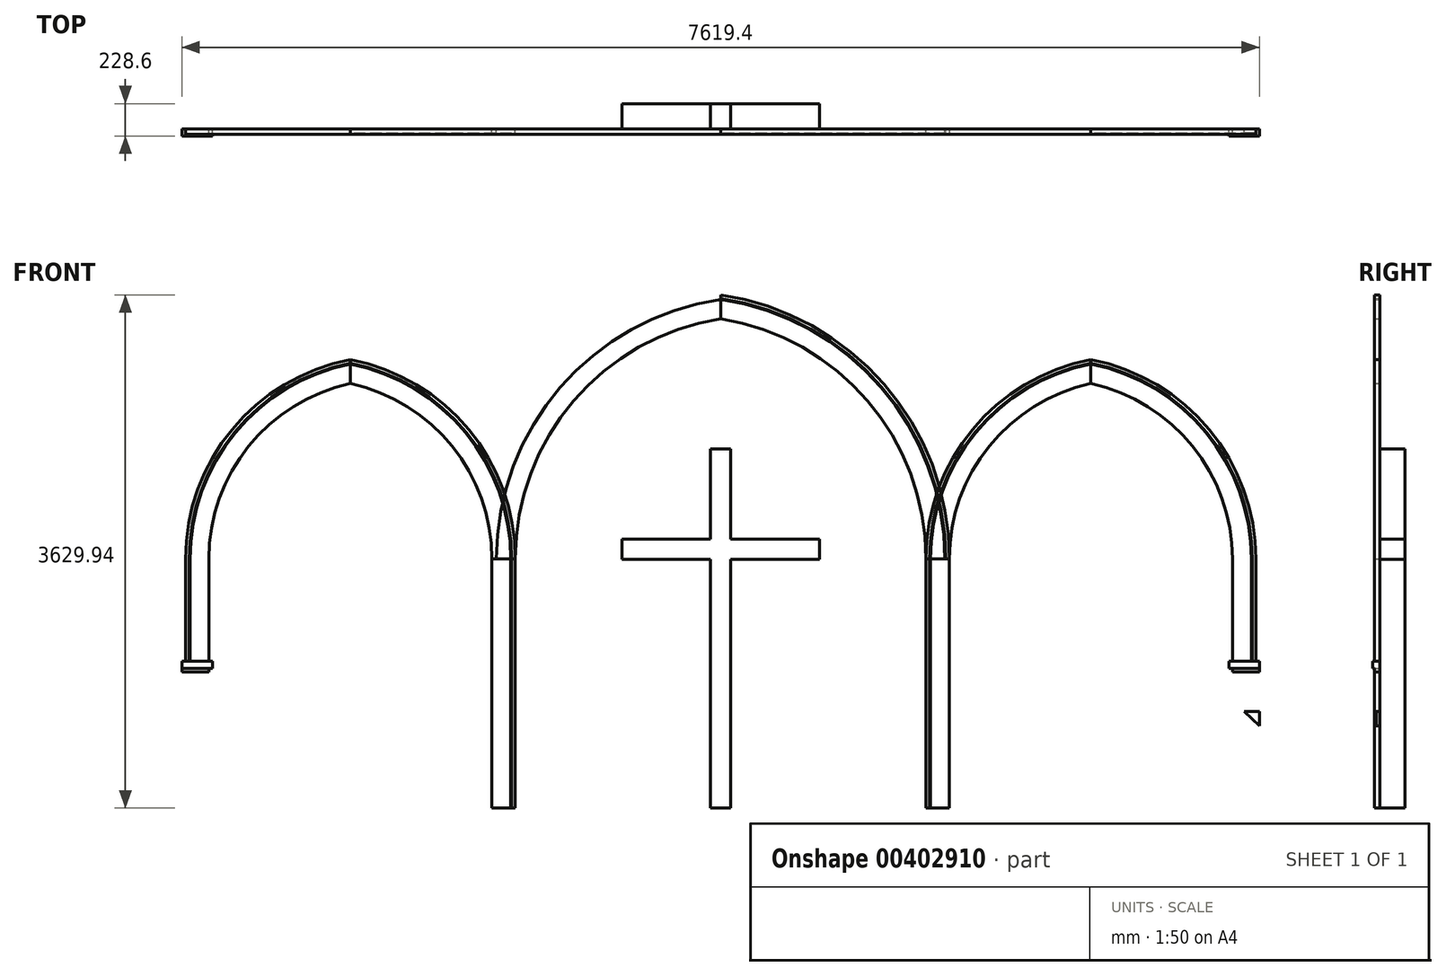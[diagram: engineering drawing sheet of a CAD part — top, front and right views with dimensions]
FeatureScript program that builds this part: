
annotation { "Feature Type Name" : "Feature", "Feature Type Description" : "" }
export const myFeature = defineFeature(function(context is Context, id is Id, definition is map)
    precondition{}
    {
        {
            var Q0;
            Q0=qCreatedBy(makeId("Front.planeOp"),FACE);
            var sketch = newSketch(context, id + "F0", { "sketchPlane" : qUnion([Q0])});
            skLineSegment(sketch, "E0", {"start": v(0, 0) * mm, "end": v(986.7, 0) * mm, "construction": true});
            skLineSegment(sketch, "E1", {"start": v(986.7, 0) * mm, "end": v(986.7, 0) * mm});
            skArc(sketch, "E2", {"start": v(986.7, 0) * mm, "mid": v(709.41, 787.09) * mm, "end": v(0, 1226.56) * mm, "construction": true});
            skLineSegment(sketch, "E3", {"start": v(0, 0) * mm, "end": v(0, 1226.56) * mm, "construction": true});
            skArc(sketch, "E4", {"start": v(1120.06, 0) * mm, "mid": v(804.11, 882) * mm, "end": v(0, 1362.77) * mm, "construction": true});
            skArc(sketch, "E5", {"start": v(1126.4, 0) * mm, "mid": v(808.62, 886.51) * mm, "end": v(0, 1369.24) * mm, "construction": true});
            skArc(sketch, "E6", {"start": v(1151.8, 0) * mm, "mid": v(826.65, 904.57) * mm, "end": v(0, 1395.11) * mm, "construction": true});
            skLineSegment(sketch, "E7", {"start": v(986.7, 0) * mm, "end": v(1120.06, 0) * mm, "construction": true});
            skLineSegment(sketch, "E8", {"start": v(1120.06, 0) * mm, "end": v(1126.4, 0) * mm, "construction": true});
            skLineSegment(sketch, "E9", {"start": v(1126.4, 0) * mm, "end": v(1151.8, 0) * mm, "construction": true});
            skSolve(sketch);
        }
        {
            var Q0;
            Q0=qCreatedBy(makeId("Front.planeOp"),FACE);
            var sketch = newSketch(context, id + "F1", { "sketchPlane" : qUnion([Q0])});
            skArc(sketch, "E10", {"start": v(1452.06, 0) * mm, "mid": v(1039.63, 1117.83) * mm, "end": v(0, 1699.91) * mm});
            skArc(sketch, "E11", {"start": v(1585.41, 0) * mm, "mid": v(1134.15, 1212.44) * mm, "end": v(0, 1834.8) * mm});
            skArc(sketch, "E12", {"start": v(1591.76, 0) * mm, "mid": v(1138.65, 1216.94) * mm, "end": v(0, 1841.22) * mm});
            skArc(sketch, "E13", {"start": v(1617.16, 0) * mm, "mid": v(1156.65, 1234.96) * mm, "end": v(0, 1866.89) * mm});
            skLineSegment(sketch, "E14", {"start": v(1452.06, 0) * mm, "end": v(1585.41, 0) * mm, "construction": true});
            skLineSegment(sketch, "E15", {"start": v(1585.41, 0) * mm, "end": v(1591.76, 0) * mm, "construction": true});
            skLineSegment(sketch, "E16", {"start": v(1591.76, 0) * mm, "end": v(1617.16, 0) * mm, "construction": true});
            skLineSegment(sketch, "E17", {"start": v(0, 1866.89) * mm, "end": v(0, 1699.91) * mm});
            skLineSegment(sketch, "E18", {"start": v(1452.06, 0) * mm, "end": v(1617.16, 0) * mm});
            skSolve(sketch);
        }
        {
            var Q0;
            Q0=qCreatedBy(makeId("Front.planeOp"),FACE);
            var sketch = newSketch(context, id + "F2", { "sketchPlane" : qUnion([Q0])});
            skLineSegment(sketch, "E19.bottom", {"start": v(71.44, 776.95) * mm, "end": v(-71.44, 776.95) * mm});
            skLineSegment(sketch, "E19.top", {"start": v(71.44, -1763.05) * mm, "end": v(-71.44, -1763.05) * mm});
            skLineSegment(sketch, "E19.left", {"start": v(71.44, 776.95) * mm, "end": v(71.44, -1763.05) * mm});
            skLineSegment(sketch, "E19.right", {"start": v(-71.44, 776.95) * mm, "end": v(-71.44, -1763.05) * mm});
            skPoint(sketch, "E19.middle", {"position": v(0, -493.05) * mm});
            skLineSegment(sketch, "E20.bottom", {"start": v(698.5, 138.78) * mm, "end": v(-698.5, 138.78) * mm});
            skLineSegment(sketch, "E20.top", {"start": v(698.5, -4.1) * mm, "end": v(-698.5, -4.1) * mm});
            skLineSegment(sketch, "E20.left", {"start": v(698.5, 138.78) * mm, "end": v(698.5, -4.1) * mm});
            skLineSegment(sketch, "E20.right", {"start": v(-698.5, 138.78) * mm, "end": v(-698.5, -4.1) * mm});
            skPoint(sketch, "E20.middle", {"position": v(0, 67.34) * mm});
            skSolve(sketch);
        }
        {
            var Q0;
            Q0=qCreatedBy(makeId("Front.planeOp"),FACE);
            var sketch = newSketch(context, id + "F3", { "sketchPlane" : qUnion([Q0])});
            skLineSegment(sketch, "E21", {"start": v(2618.18, 0) * mm, "end": v(3604.88, 0) * mm, "construction": true});
            skArc(sketch, "E22", {"start": v(3604.88, 0) * mm, "mid": v(3327.6, 787.09) * mm, "end": v(2618.18, 1226.56) * mm, "construction": true});
            skLineSegment(sketch, "E23", {"start": v(2618.18, 0) * mm, "end": v(2618.18, 1226.56) * mm, "construction": true});
            skArc(sketch, "E24", {"start": v(3738.23, 0) * mm, "mid": v(3422.29, 882) * mm, "end": v(2618.18, 1362.77) * mm, "construction": true});
            skArc(sketch, "E25", {"start": v(3744.58, 0) * mm, "mid": v(3426.8, 886.51) * mm, "end": v(2618.18, 1369.24) * mm, "construction": true});
            skArc(sketch, "E26", {"start": v(3769.98, 0) * mm, "mid": v(3444.83, 904.57) * mm, "end": v(2618.18, 1395.11) * mm, "construction": true});
            skLineSegment(sketch, "E27", {"start": v(3604.88, 0) * mm, "end": v(3738.23, 0) * mm, "construction": true});
            skLineSegment(sketch, "E28", {"start": v(3738.23, 0) * mm, "end": v(3744.58, 0) * mm, "construction": true});
            skLineSegment(sketch, "E29", {"start": v(3744.58, 0) * mm, "end": v(3769.98, 0) * mm, "construction": true});
            skLineSegment(sketch, "E30", {"start": v(2349.17, 0) * mm, "end": v(2618.18, 0) * mm, "construction": true});
            skLineSegment(sketch, "E31", {"start": v(2618.18, 1226.56) * mm, "end": v(2618.18, 1362.77) * mm, "construction": true});
            skLineSegment(sketch, "E32", {"start": v(2618.18, 1362.77) * mm, "end": v(2618.18, 1369.24) * mm, "construction": true});
            skLineSegment(sketch, "E33", {"start": v(2618.18, 1369.24) * mm, "end": v(2618.18, 1395.11) * mm, "construction": true});
            skArc(sketch, "E34", {"start": v(3619.2, 0) * mm, "mid": v(3337.76, 797.28) * mm, "end": v(2618.18, 1241.2) * mm});
            skArc(sketch, "E35", {"start": v(3752.55, 0) * mm, "mid": v(3432.45, 892.17) * mm, "end": v(2618.18, 1377.35) * mm});
            skArc(sketch, "E36", {"start": v(3758.9, 0) * mm, "mid": v(3436.96, 896.69) * mm, "end": v(2618.18, 1383.82) * mm});
            skArc(sketch, "E37", {"start": v(3784.3, 0) * mm, "mid": v(3454.98, 914.75) * mm, "end": v(2618.18, 1409.69) * mm});
            skLineSegment(sketch, "E38", {"start": v(3619.2, 0) * mm, "end": v(3752.55, 0) * mm, "construction": true});
            skLineSegment(sketch, "E39", {"start": v(3752.55, 0) * mm, "end": v(3758.9, 0) * mm, "construction": true});
            skLineSegment(sketch, "E40", {"start": v(3758.9, 0) * mm, "end": v(3784.3, 0) * mm, "construction": true});
            skLineSegment(sketch, "E41", {"start": v(3619.2, 0) * mm, "end": v(3784.3, 0) * mm});
            skLineSegment(sketch, "E42", {"start": v(2618.18, 1241.2) * mm, "end": v(2618.18, 1409.69) * mm});
            skLineSegment(sketch, "E43", {"start": v(2618.18, -162.35) * mm, "end": v(3784.3, -162.35) * mm, "construction": true});
            skLineSegment(sketch, "E44", {"start": v(2618.18, 0) * mm, "end": v(1452.06, 0) * mm, "construction": true});
            skPoint(sketch, "E44.endSnap0", {"position": v(2483.68, 0) * mm});
            skSolve(sketch);
        }
        {
            var Q0;
            {var subQ0=sQuery(id+"F1.wireOp",EDGE,"E10");Q0=makeQuery(id+"F1.imprint","IMPRINT",FACE,{"disambiguationData":[TD([[makeQuery(id+"F1.imprint","IMPRINT",EDGE,{"derivedFrom":subQ0}),-1.0]])]});}
            var Q1;
            {var subQ0=sQuery(id+"F1.wireOp",EDGE,"E12");Q1=makeQuery(id+"F1.imprint","IMPRINT",FACE,{"disambiguationData":[TD([[makeQuery(id+"F1.imprint","IMPRINT",EDGE,{"derivedFrom":subQ0}),-1.0]])]});}
            extrude(context, id + "F4", {"entities" : qUnion([Q0, Q1]), "depth" : 38.1 * mm});
        }
        {
            var Q0;
            {var subQ0=sQuery(id+"F1.wireOp",EDGE,"E11");Q0=makeQuery(id+"F1.imprint","IMPRINT",FACE,{"disambiguationData":[TD([[makeQuery(id+"F1.imprint","IMPRINT",EDGE,{"derivedFrom":subQ0}),-1.0]])]});}
            extrude(context, id + "F5", {"entities" : qUnion([Q0]), "depth" : 31.75 * mm});
        }
        {
            var Q0;
            {var subQ0=sQuery(id+"F3.wireOp",EDGE,"E36");Q0=makeQuery(id+"F3.imprint","IMPRINT",FACE,{"disambiguationData":[TD([[makeQuery(id+"F3.imprint","IMPRINT",EDGE,{"derivedFrom":subQ0}),-1.0]])]});}
            var Q1;
            {var subQ0=sQuery(id+"F3.wireOp",EDGE,"E34");Q1=makeQuery(id+"F3.imprint","IMPRINT",FACE,{"disambiguationData":[TD([[makeQuery(id+"F3.imprint","IMPRINT",EDGE,{"derivedFrom":subQ0}),-1.0]])]});}
            extrude(context, id + "F6", {"entities" : qUnion([Q0, Q1]), "depth" : 38.1 * mm});
        }
        {
            var Q0;
            {var subQ0=sQuery(id+"F3.wireOp",EDGE,"E35");Q0=makeQuery(id+"F3.imprint","IMPRINT",FACE,{"disambiguationData":[TD([[makeQuery(id+"F3.imprint","IMPRINT",EDGE,{"derivedFrom":subQ0}),-1.0]])]});}
            extrude(context, id + "F7", {"entities" : qUnion([Q0]), "depth" : 31.75 * mm});
        }
        {
            var Q0;
            Q0=makeQuery(id+"F6.opExtrude","SWEPT_BODY",BODY,{"disambiguationData":[OSD([sQuery(id+"F3.wireOp",EDGE,"E34"),sQuery(id+"F3.wireOp",EDGE,"E35"),sQuery(id+"F3.wireOp",EDGE,"E41"),sQuery(id+"F3.wireOp",EDGE,"E42")])]});
            var Q1;
            Q1=makeQuery(id+"F6.opExtrude","SWEPT_BODY",BODY,{"disambiguationData":[OSD([sQuery(id+"F3.wireOp",EDGE,"E36"),sQuery(id+"F3.wireOp",EDGE,"E37"),sQuery(id+"F3.wireOp",EDGE,"E41"),sQuery(id+"F3.wireOp",EDGE,"E42")])]});
            var Q2;
            Q2=makeQuery(id+"F7.opExtrude","SWEPT_BODY",BODY,{"disambiguationData":[OSD([sQuery(id+"F3.wireOp",EDGE,"E35"),sQuery(id+"F3.wireOp",EDGE,"E36"),sQuery(id+"F3.wireOp",EDGE,"E41"),sQuery(id+"F3.wireOp",EDGE,"E42")])]});
            booleanBodies(context, id + "F8", {"operationType" : BooleanOperationType.UNION, "tools" : qUnion([Q0, Q1, Q2])});
        }
        {
            var Q0;
            Q0=makeQuery(id+"F6.opExtrude","SWEPT_BODY",BODY,{"disambiguationData":[OSD([sQuery(id+"F3.wireOp",EDGE,"E34"),sQuery(id+"F3.wireOp",EDGE,"E35"),sQuery(id+"F3.wireOp",EDGE,"E41"),sQuery(id+"F3.wireOp",EDGE,"E42")])]});
            var Q1;
            {var subQ0=sQuery(id+"F3.wireOp",EDGE,"E42");Q1=makeQuery(id+"F8.opBoolean","MERGE",FACE,{"derivedFrom":[makeQuery(id+"F6.opExtrude","SWEPT_FACE",FACE,{"disambiguationData":[OSD([subQ0]),TDD([makeQuery(id+"F3.imprint","IMPRINT",EDGE,{"disambiguationData":[TD([[makeQuery(id+"F3.imprint","INTERSECT",VERTEX,{"derivedFrom":[sQuery(id+"F3.wireOp",EDGE,"E34"),subQ0]}),-1.0]])],"derivedFrom":subQ0})])]}),makeQuery(id+"F6.opExtrude","SWEPT_FACE",FACE,{"disambiguationData":[OSD([subQ0]),TDD([makeQuery(id+"F3.imprint","IMPRINT",EDGE,{"disambiguationData":[TD([[makeQuery(id+"F3.imprint","INTERSECT",VERTEX,{"derivedFrom":[sQuery(id+"F3.wireOp",EDGE,"E36"),subQ0]}),-1.0]])],"derivedFrom":subQ0})])]}),makeQuery(id+"F7.opExtrude","SWEPT_FACE",FACE,{"disambiguationData":[OSD([subQ0])]})]});}
            mirror(context, id + "F9", {"entities" : qUnion([Q0]), "mirrorPlane" : qUnion([Q1])});
        }
        {
            var Q0;
            Q0=qSketchRegion(id+"F2",true);
            extrude(context, id + "F10", {"entities" : qUnion([Q0]), "oppositeDirection" : true, "depth" : 177.8 * mm});
        }
        {
            var Q0;
            Q0=qCreatedBy(makeId("Front.planeOp"),FACE);
            var sketch = newSketch(context, id + "F11", { "sketchPlane" : qUnion([Q0])});
            skLineSegment(sketch, "E45", {"start": v(3619.2, -723.91) * mm, "end": v(3593.8, -723.91) * mm});
            skLineSegment(sketch, "E46", {"start": v(3593.8, -723.91) * mm, "end": v(3593.8, -800.11) * mm});
            skLineSegment(sketch, "E47", {"start": v(3593.8, -800.11) * mm, "end": v(3809.7, -800.11) * mm});
            skLineSegment(sketch, "E48", {"start": v(3809.7, -800.11) * mm, "end": v(3809.7, -723.91) * mm});
            skLineSegment(sketch, "E49", {"start": v(3809.7, -723.91) * mm, "end": v(3784.3, -723.91) * mm});
            skPoint(sketch, "E50.oppositeSnap0", {"position": v(3701.75, -800.11) * mm});
            skLineSegment(sketch, "E50.bottom", {"start": v(3809.7, -800.11) * mm, "end": v(3701.75, -800.11) * mm});
            skLineSegment(sketch, "E50.top", {"start": v(3809.7, -1079.51) * mm, "end": v(3701.75, -1079.51) * mm});
            skLineSegment(sketch, "E50.left", {"start": v(3809.7, -800.11) * mm, "end": v(3809.7, -1079.51) * mm});
            skLineSegment(sketch, "E50.right", {"start": v(3701.75, -800.11) * mm, "end": v(3701.75, -1079.51) * mm});
            skLineSegment(sketch, "E51", {"start": v(3809.7, -1181.11) * mm, "end": v(3809.7, -1079.51) * mm});
            skLineSegment(sketch, "E52", {"start": v(3701.75, -1079.51) * mm, "end": v(3809.7, -1181.11) * mm});
            skLineSegment(sketch, "E53", {"start": v(3593.8, -774.71) * mm, "end": v(3619.2, -774.71) * mm});
            skLineSegment(sketch, "E54", {"start": v(3619.2, -774.71) * mm, "end": v(3619.2, -800.11) * mm});
            skLineSegment(sketch, "E55.bottom", {"start": v(3619.2, 0) * mm, "end": v(3784.3, 0) * mm});
            skLineSegment(sketch, "E55.top", {"start": v(3619.2, -723.91) * mm, "end": v(3784.3, -723.91) * mm});
            skLineSegment(sketch, "E55.left", {"start": v(3619.2, 0) * mm, "end": v(3619.2, -723.91) * mm});
            skLineSegment(sketch, "E55.right", {"start": v(3784.3, 0) * mm, "end": v(3784.3, -723.91) * mm});
            skSolve(sketch);
        }
        {
            var Q0;
            Q0=makeQuery(id+"F11.imprint","IMPRINT",FACE,{"disambiguationData":[TD([[makeQuery(id+"F11.imprint","IMPRINT",EDGE,{"derivedFrom":sQuery(id+"F11.wireOp",EDGE,"E45")}),1.0]])]});
            extrude(context, id + "F12", {"entities" : qUnion([Q0]), "operationType" : NewBodyOperationType.ADD, "depth" : 50.8 * mm});
        }
        {
            var Q0;
            Q0=makeQuery(id+"F11.imprint","IMPRINT",FACE,{"disambiguationData":[TD([[makeQuery(id+"F11.imprint","IMPRINT",EDGE,{"derivedFrom":sQuery(id+"F11.wireOp",EDGE,"E50.bottom")}),1.0]])]});
            var Q1;
            Q1=makeQuery(id+"F11.imprint","IMPRINT",FACE,{"disambiguationData":[TD([[makeQuery(id+"F11.imprint","IMPRINT",EDGE,{"derivedFrom":sQuery(id+"F11.wireOp",EDGE,"E50.top")}),1.0]])]});
            extrude(context, id + "F13", {"entities" : qUnion([Q0, Q1]), "operationType" : NewBodyOperationType.ADD, "depth" : 25.4 * mm});
        }
        {
            var Q0;
            Q0=makeQuery(id+"F12.opExtrude","CAP_FACE",FACE,{"disambiguationData":[OSD([sQuery(id+"F11.wireOp",EDGE,"E45"),sQuery(id+"F11.wireOp",EDGE,"E46"),sQuery(id+"F11.wireOp",EDGE,"E47"),sQuery(id+"F11.wireOp",EDGE,"E48"),sQuery(id+"F11.wireOp",EDGE,"E49"),sQuery(id+"F11.wireOp",EDGE,"EU8AyILK-9z8Q-gdrX-oHTT-qgVQCwwBBT7s"),sQuery(id+"F11.wireOp",EDGE,"E50.bottom"),sQuery(id+"F11.wireOp",EDGE,"E53"),sQuery(id+"F11.wireOp",EDGE,"E54")])],"isStart":false});
            var sketch = newSketch(context, id + "F14", { "sketchPlane" : qUnion([Q0])});
            skLineSegment(sketch, "E56", {"start": v(3619.2, -774.71) * mm, "end": v(3809.7, -774.71) * mm});
            skSolve(sketch);
        }
        {
            var Q0;
            {var subQ0=sQuery(id+"F14.wireOp",EDGE,"E56");Q0=makeQuery(id+"F14.imprint","IMPRINT",FACE,{"disambiguationData":[TD([[makeQuery(id+"F14.imprint","IMPRINT",EDGE,{"derivedFrom":subQ0}),-1.0]])]});}
            extrude(context, id + "F15", {"entities" : qUnion([Q0]), "operationType" : NewBodyOperationType.REMOVE, "oppositeDirection" : true, "depth" : 12.7 * mm});
        }
        {
            var Q0;
            Q0=makeQuery(id+"F11.imprint","IMPRINT",FACE,{"disambiguationData":[TD([[makeQuery(id+"F11.imprint","IMPRINT",EDGE,{"derivedFrom":sQuery(id+"F11.wireOp",EDGE,"E55.bottom")}),-1.0]])]});
            var Q1;
            Q1=makeQuery(id+"F6.opExtrude","CAP_FACE",FACE,{"disambiguationData":[OSD([sQuery(id+"F3.wireOp",EDGE,"E34"),sQuery(id+"F3.wireOp",EDGE,"E35"),sQuery(id+"F3.wireOp",EDGE,"E41"),sQuery(id+"F3.wireOp",EDGE,"E42")])],"isStart":false});
            extrude(context, id + "F16", {"entities" : qUnion([Q0]), "operationType" : NewBodyOperationType.ADD, "endBound" : BoundingType.UP_TO_SURFACE, "endBoundEntityFace" : qUnion([Q1]), "depth" : 25.4 * mm});
        }
        {
            var Q0;
            {var subQ0=sQuery(id+"F3.wireOp",EDGE,"E42");var subQ1=sQuery(id+"F3.wireOp",EDGE,"E41");Q0=makeQuery(id+"F16.boolean.opBoolean","MERGE",FACE,{"derivedFrom":[makeQuery(id+"F6.opExtrude","CAP_FACE",FACE,{"disambiguationData":[OSD([sQuery(id+"F3.wireOp",EDGE,"E34"),sQuery(id+"F3.wireOp",EDGE,"E35"),subQ1,subQ0])],"isStart":false}),makeQuery(id+"F6.opExtrude","CAP_FACE",FACE,{"disambiguationData":[OSD([sQuery(id+"F3.wireOp",EDGE,"E36"),sQuery(id+"F3.wireOp",EDGE,"E37"),subQ1,subQ0])],"isStart":false}),makeQuery(id+"F16.opExtrude","CAP_FACE",FACE,{"disambiguationData":[OSD([sQuery(id+"F11.wireOp",EDGE,"E55.bottom"),sQuery(id+"F11.wireOp",EDGE,"E55.top"),sQuery(id+"F11.wireOp",EDGE,"E55.left"),sQuery(id+"F11.wireOp",EDGE,"E55.right")])],"isStart":false})]});}
            var sketch = newSketch(context, id + "F17", { "sketchPlane" : qUnion([Q0])});
            skLineSegment(sketch, "E57", {"start": v(3752.55, 0) * mm, "end": v(3752.55, -723.91) * mm});
            skLineSegment(sketch, "E58", {"start": v(3752.55, -723.91) * mm, "end": v(3758.9, -723.91) * mm});
            skLineSegment(sketch, "E59", {"start": v(3758.9, -723.91) * mm, "end": v(3758.9, 0) * mm});
            skLineSegment(sketch, "E60", {"start": v(3758.9, 0) * mm, "end": v(3752.55, 0) * mm});
            skSolve(sketch);
        }
        {
            var Q0;
            Q0=makeQuery(id+"F17.imprint","IMPRINT",FACE,{"disambiguationData":[TD([[makeQuery(id+"F17.imprint","IMPRINT",EDGE,{"derivedFrom":sQuery(id+"F17.wireOp",EDGE,"E57")}),1.0]])]});
            var Q1;
            Q1=makeQuery(id+"F7.opExtrude","CAP_FACE",FACE,{"disambiguationData":[OSD([sQuery(id+"F3.wireOp",EDGE,"E35"),sQuery(id+"F3.wireOp",EDGE,"E36"),sQuery(id+"F3.wireOp",EDGE,"E41"),sQuery(id+"F3.wireOp",EDGE,"E42")])],"isStart":false});
            extrude(context, id + "F18", {"entities" : qUnion([Q0]), "operationType" : NewBodyOperationType.REMOVE, "endBound" : BoundingType.UP_TO_SURFACE, "oppositeDirection" : true, "endBoundEntityFace" : qUnion([Q1]), "depth" : 25.4 * mm});
        }
        {
            var Q0;
            Q0=makeQuery(id+"F12.opExtrude","CAP_FACE",FACE,{"disambiguationData":[OSD([sQuery(id+"F11.wireOp",EDGE,"E45"),sQuery(id+"F11.wireOp",EDGE,"E46"),sQuery(id+"F11.wireOp",EDGE,"E47"),sQuery(id+"F11.wireOp",EDGE,"E48"),sQuery(id+"F11.wireOp",EDGE,"E49"),sQuery(id+"F11.wireOp",EDGE,"E50.bottom"),sQuery(id+"F11.wireOp",EDGE,"E53"),sQuery(id+"F11.wireOp",EDGE,"E54"),sQuery(id+"F11.wireOp",EDGE,"E55.top")])],"isStart":false});
            var sketch = newSketch(context, id + "F19", { "sketchPlane" : qUnion([Q0])});
            skLineSegment(sketch, "E61.bottom", {"start": v(3619.2, -774.71) * mm, "end": v(3809.7, -774.71) * mm});
            skLineSegment(sketch, "E61.top", {"start": v(3619.2, -800.11) * mm, "end": v(3809.7, -800.11) * mm});
            skLineSegment(sketch, "E61.left", {"start": v(3619.2, -774.71) * mm, "end": v(3619.2, -800.11) * mm});
            skLineSegment(sketch, "E61.right", {"start": v(3809.7, -774.71) * mm, "end": v(3809.7, -800.11) * mm});
            skSolve(sketch);
        }
        {
            var Q0;
            {var subQ0=sQuery(id+"F3.wireOp",EDGE,"E41");Q0=makeQuery(id+"F9.opPattern","COPY",FACE,{"derivedFrom":makeQuery(id+"F8.opBoolean","MERGE",FACE,{"derivedFrom":[makeQuery(id+"F6.opExtrude","SWEPT_FACE",FACE,{"disambiguationData":[OSD([subQ0]),TDD([makeQuery(id+"F3.imprint","IMPRINT",EDGE,{"disambiguationData":[TD([[makeQuery(id+"F3.imprint","INTERSECT",VERTEX,{"derivedFrom":[sQuery(id+"F3.wireOp",EDGE,"E34"),subQ0]}),-1.0]])],"derivedFrom":subQ0})])]}),makeQuery(id+"F6.opExtrude","SWEPT_FACE",FACE,{"disambiguationData":[OSD([subQ0]),TDD([makeQuery(id+"F3.imprint","IMPRINT",EDGE,{"disambiguationData":[TD([[makeQuery(id+"F3.imprint","INTERSECT",VERTEX,{"derivedFrom":[sQuery(id+"F3.wireOp",EDGE,"E36"),subQ0]}),-1.0]])],"derivedFrom":subQ0})])]}),makeQuery(id+"F7.opExtrude","SWEPT_FACE",FACE,{"disambiguationData":[OSD([subQ0])]})]}),"instanceName":"1"});}
            var Q1;
            Q1=makeQuery(id+"F10.opExtrude","SWEPT_FACE",FACE,{"disambiguationData":[OSD([sQuery(id+"F2.wireOp",EDGE,"E19.top")])]});
            extrude(context, id + "F20", {"entities" : qUnion([Q0]), "endBound" : BoundingType.UP_TO_SURFACE, "endBoundEntityFace" : qUnion([Q1]), "depth" : 25.4 * mm});
        }
        {
            var Q0;
            Q0=makeQuery(id+"F19.imprint","IMPRINT",FACE,{"disambiguationData":[TD([[makeQuery(id+"F19.imprint","IMPRINT",EDGE,{"derivedFrom":sQuery(id+"F19.wireOp",EDGE,"E61.bottom")}),-1.0]])]});
            extrude(context, id + "F21", {"entities" : qUnion([Q0]), "operationType" : NewBodyOperationType.REMOVE, "oppositeDirection" : true, "depth" : 12.7 * mm});
        }
        {
            var Q0;
            Q0=makeQuery(id+"F12.opExtrude","SWEPT_BODY",BODY,{"disambiguationData":[OSD([sQuery(id+"F11.wireOp",EDGE,"E45"),sQuery(id+"F11.wireOp",EDGE,"E46"),sQuery(id+"F11.wireOp",EDGE,"E47"),sQuery(id+"F11.wireOp",EDGE,"E48"),sQuery(id+"F11.wireOp",EDGE,"E49"),sQuery(id+"F11.wireOp",EDGE,"E50.bottom"),sQuery(id+"F11.wireOp",EDGE,"E53"),sQuery(id+"F11.wireOp",EDGE,"E54"),sQuery(id+"F11.wireOp",EDGE,"E55.top")])]});
            var Q1;
            Q1=makeQuery(id+"F4.opExtrude","SWEPT_BODY",BODY,{"disambiguationData":[OSD([sQuery(id+"F1.wireOp",EDGE,"E10"),sQuery(id+"F1.wireOp",EDGE,"E11"),sQuery(id+"F1.wireOp",EDGE,"E17"),sQuery(id+"F1.wireOp",EDGE,"E18")])]});
            var Q2;
            Q2=makeQuery(id+"F9.opPattern","COPY",BODY,{"derivedFrom":makeQuery(id+"F6.opExtrude","SWEPT_BODY",BODY,{"disambiguationData":[OSD([sQuery(id+"F3.wireOp",EDGE,"E34"),sQuery(id+"F3.wireOp",EDGE,"E35"),sQuery(id+"F3.wireOp",EDGE,"E41"),sQuery(id+"F3.wireOp",EDGE,"E42")])]}),"instanceName":"1"});
            var Q3;
            Q3=makeQuery(id+"F6.opExtrude","SWEPT_BODY",BODY,{"disambiguationData":[OSD([sQuery(id+"F3.wireOp",EDGE,"E34"),sQuery(id+"F3.wireOp",EDGE,"E35"),sQuery(id+"F3.wireOp",EDGE,"E41"),sQuery(id+"F3.wireOp",EDGE,"E42")])]});
            var Q4;
            Q4=makeQuery(id+"F20.opExtrude","SWEPT_BODY",BODY,{"disambiguationData":[OSD([sQuery(id+"F3.wireOp",EDGE,"E41")])]});
            var Q5;
            Q5=qCreatedBy(makeId("Right.planeOp"),FACE);
            mirror(context, id + "F22", {"entities" : qUnion([Q0, Q1, Q2, Q3, Q4]), "mirrorPlane" : qUnion([Q5])});
        }
    });
